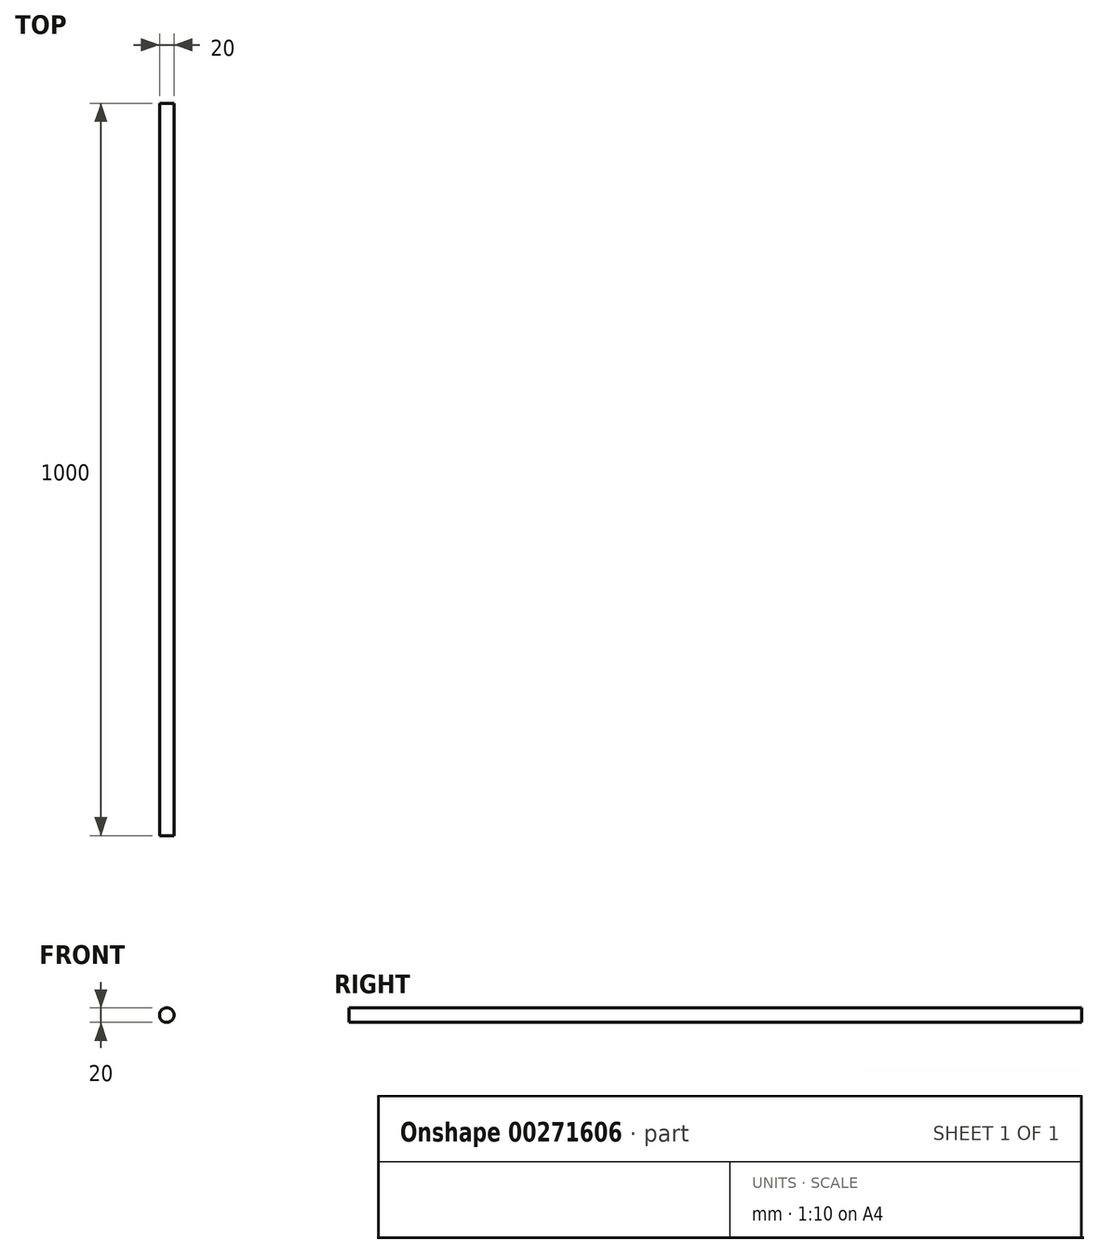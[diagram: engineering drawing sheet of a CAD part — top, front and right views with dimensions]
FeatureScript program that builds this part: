
annotation { "Feature Type Name" : "Feature", "Feature Type Description" : "" }
export const myFeature = defineFeature(function(context is Context, id is Id, definition is map)
    precondition{}
    {
        {
            var Q0;
            Q0=qCreatedBy(makeId("Front.planeOp"),FACE);
            var sketch = newSketch(context, id + "F0", { "sketchPlane" : qUnion([Q0])});
            skCircle(sketch, "E0", {"center": v(0, 0) * mm, "radius": 10 * mm});
            skSolve(sketch);
        }
        {
            var Q0;
            Q0=makeQuery(id+"F0.imprint","IMPRINT",FACE,{"disambiguationData":[TD([[makeQuery(id+"F0.imprint","IMPRINT",EDGE,{"derivedFrom":sQuery(id+"F0.wireOp",EDGE,"E0")}),1.0]])]});
            var Q1;
            Q1=sQuery(id+"F0.wireOp",EDGE,"E0");
            extrude(context, id + "F1", {"entities" : qUnion([Q0]), "surfaceEntities" : qUnion([Q1]), "depth" : 1000 * mm});
        }
    });
